# Revit family: EDD
name_source: partatom
category: Mechanical Equipment
units: mm (PartAtom-declared; Revit-internal decimal feet)

## family parameters
Always vertical = Yes
Cut with Voids When Loaded = No
Part Type = Normal
Room Calculation Point = No
Round Connector Dimension = Use Radius
Shared = No
Work Plane-Based = No

## types (5) — shared parameters
0 = 0' - 0"
1" = 0' - 1"
1.5 = 0' - 1 1/2"
103 = 103.00°
135 = 135.00°
160 = 160.00°
2" = 0' - 2"
2' = 2' - 0"
3" = 0' - 3"
4" = 0' - 4"
60 = 30.00°
Manufacturer = Loren Cook Company
Model = EDD
ONE EIGTH = 0' - 0 1/8"
Type Comments = Tube Axial Drum Fan Extruded Aluminum Propeller Direct Drive
URL = www.lorencook.com

## per-type parameters (varying)
| type | (B-C)-1" | (B/2)-C | (B/2)-C+.125" | -A/2 | -A/3*2 | -E | -G | A | A/2 | A/3*2 | B | B/2 | B/3 | B/6 | C | C/2 | D | E | F | F/2 | G | H | J | J/2 |
| 24_EDD | 1' - 0" | 1' - 0 1/4" | 1' - 0 3/8" | -0' - 11 1/2" | -0' - 10 21/32" | -1' - 8" | -0' - 5 1/4" | 1' - 7" | 0' - 9 1/2" | 0' - 10 21/32" | 2' - 3 1/2" | 1' - 1 3/4" | 0' - 9 5/32" | 0' - 4 19/32" | 0' - 1 1/2" | 0' - 0 3/4" | 1' - 5 1/8" | 1' - 8" | 1' - 4 1/8" | 0' - 8 1/16" | 0' - 5 1/4" | 1' - 4 5/16" | 0' - 9 3/4" | 0' - 4 7/8" |
| 30_EDD | 1' - 3" | 1' - 3 1/4" | 1' - 3 3/8" | -1' - 0 1/2" | -1' - 0" | -1' - 10" | -0' - 5 1/4" | 1' - 9" | 0' - 10 1/2" | 1' - 0" | 2' - 9 1/2" | 1' - 4 3/4" | 0' - 11 5/32" | 0' - 5 19/32" | 0' - 1 1/2" | 0' - 0 3/4" | 1' - 10 1/8" | 1' - 10" | 1' - 6 1/8" | 0' - 9 1/16" | 0' - 5 1/4" | 1' - 4 5/16" | 0' - 9 3/4" | 0' - 4 7/8" |
| 36_EDD | 1' - 6" | 1' - 6 1/4" | 1' - 6 3/8" | -1' - 0 1/2" | -1' - 0" | -2' - 1" | -0' - 6 3/4" | 1' - 9" | 0' - 10 1/2" | 1' - 0" | 3' - 3 1/2" | 1' - 7 3/4" | 1' - 1 5/32" | 0' - 6 19/32" | 0' - 1 1/2" | 0' - 0 3/4" | 1' - 10 1/8" | 2' - 1" | 1' - 9 1/8" | 0' - 10 9/16" | 0' - 6 3/4" | 1' - 5 13/16" | 1' - 0 3/4" | 0' - 6 3/8" |
| 42_EDD | 1' - 9 1/16" | 1' - 9 1/4" | 1' - 9 3/8" | -1' - 3 1/2" | -1' - 4" | -2' - 5" | -0' - 6 3/4" | 2' - 3" | 1' - 1 1/2" | 1' - 4" | 3' - 9 3/4" | 1' - 10 7/8" | 1' - 3 1/4" | 0' - 7 5/8" | 0' - 1 5/8" | 0' - 0 13/16" | 1' - 10 1/8" | 2' - 5" | 1' - 9 1/8" | 0' - 10 9/16" | 0' - 6 3/4" | 1' - 5 13/16" | 1' - 0 3/4" | 0' - 6 3/8" |
| 48_EDD | 2' - 0 5/16" | 2' - 0 1/4" | 2' - 0 3/8" | -1' - 3 1/2" | -1' - 4" | -2' - 7" | -0' - 6 3/4" | 2' - 3" | 1' - 1 1/2" | 1' - 4" | 4' - 4 3/4" | 2' - 2 3/8" | 1' - 5 19/32" | 0' - 8 25/32" | 0' - 2 1/8" | 0' - 1 1/16" | 1' - 10 1/8" | 2' - 7" | 1' - 9 1/8" | 0' - 10 9/16" | 0' - 6 3/4" | 1' - 5 13/16" | 1' - 0 3/4" | 0' - 6 3/8" |

## geometry (parser evidence)
native form markers: Sweep x2
no freeform markers — native parametric forms only
